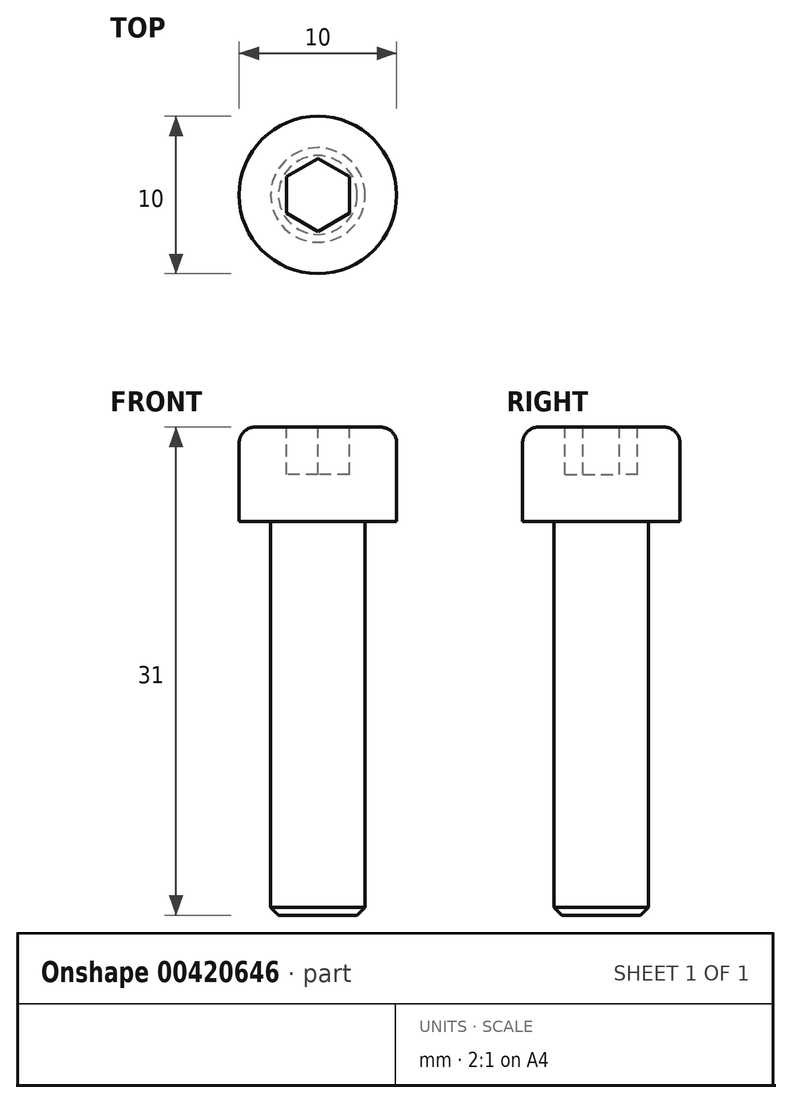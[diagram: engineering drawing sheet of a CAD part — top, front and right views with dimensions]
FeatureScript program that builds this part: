
annotation { "Feature Type Name" : "Feature", "Feature Type Description" : "" }
export const myFeature = defineFeature(function(context is Context, id is Id, definition is map)
    precondition{}
    {
        {
            var Q0;
            Q0=qCreatedBy(makeId("Front.planeOp"),FACE);
            var sketch = newSketch(context, id + "F0", { "sketchPlane" : qUnion([Q0])});
            skLineSegment(sketch, "E0", {"start": v(0, 0) * mm, "end": v(0, 31.2) * mm, "construction": true});
            skLineSegment(sketch, "E1", {"start": v(0, 0) * mm, "end": v(-3, 0) * mm});
            skLineSegment(sketch, "E2", {"start": v(-3, 0) * mm, "end": v(-3, 25) * mm});
            skLineSegment(sketch, "E3", {"start": v(-3, 25) * mm, "end": v(-5, 25) * mm});
            skLineSegment(sketch, "E4", {"start": v(-5, 25) * mm, "end": v(-5, 31) * mm});
            skLineSegment(sketch, "E5", {"start": v(-5, 31) * mm, "end": v(0, 31) * mm});
            skLineSegment(sketch, "E6", {"start": v(0, 31) * mm, "end": v(0, 0) * mm});
            skSolve(sketch);
        }
        {
            var Q0;
            Q0=makeQuery(id+"F0.imprint","IMPRINT",FACE,{"disambiguationData":[TD([[makeQuery(id+"F0.imprint","IMPRINT",EDGE,{"derivedFrom":sQuery(id+"F0.wireOp",EDGE,"E1")}),-1.0]])]});
            var Q1;
            Q1=sQuery(id+"F0.wireOp",EDGE,"E0");
            revolve(context, id + "F1", {"entities" : qUnion([Q0]), "axis" : qUnion([Q1]), "revolveType" : RevolveType.FULL});
        }
        {
            var Q0;
            Q0=makeQuery(id+"F1.opRevolve","SWEPT_EDGE",EDGE,{"disambiguationData":[OSD([sQuery(id+"F0.wireOp",EDGE,"E1"),sQuery(id+"F0.wireOp",EDGE,"E2")])]});
            chamfer(context, id + "F2", {"entities" : qUnion([Q0]), "width" : 0.5 * mm, "tangentPropagation" : true});
        }
        {
            var Q0;
            Q0=makeQuery(id+"F1.opRevolve","SWEPT_EDGE",EDGE,{"disambiguationData":[OSD([sQuery(id+"F0.wireOp",EDGE,"E4"),sQuery(id+"F0.wireOp",EDGE,"E5")])]});
            fillet(context, id + "F3", {"entities" : qUnion([Q0]), "radius" : 1 * mm, "tangentPropagation" : true, "allowEdgeOverflow" : false});
        }
        {
            var Q0;
            Q0=makeQuery(id+"F1.opRevolve","SWEPT_FACE",FACE,{"disambiguationData":[OSD([sQuery(id+"F0.wireOp",EDGE,"E5")])]});
            var sketch = newSketch(context, id + "F4", { "sketchPlane" : qUnion([Q0])});
            skCircle(sketch, "E7.cCircle", {"center": v(0, 0) * mm, "radius": 2 * mm, "construction": true});
            skLineSegment(sketch, "E7.0", {"start": v(-2, -1.15) * mm, "end": v(-2, 1.15) * mm});
            skLineSegment(sketch, "E7.1", {"start": v(-2, 1.15) * mm, "end": v(0, 2.3) * mm});
            skLineSegment(sketch, "E7.2", {"start": v(0, 2.3) * mm, "end": v(2, 1.15) * mm});
            skLineSegment(sketch, "E7.3", {"start": v(2, 1.15) * mm, "end": v(2, -1.15) * mm});
            skLineSegment(sketch, "E7.4", {"start": v(2, -1.15) * mm, "end": v(0, -2.3) * mm});
            skLineSegment(sketch, "E7.5", {"start": v(0, -2.3) * mm, "end": v(-2, -1.15) * mm});
            skPoint(sketch, "E7.0.midPoint", {"position": v(-2, 0) * mm});
            skSolve(sketch);
        }
        {
            var Q0;
            Q0 = qSketchRegion(id + "F4", true);
            extrude(context, id + "F5", {"entities" : qUnion([Q0]), "operationType" : NewBodyOperationType.REMOVE, "oppositeDirection" : true, "depth" : 3 * mm});
        }
    });
